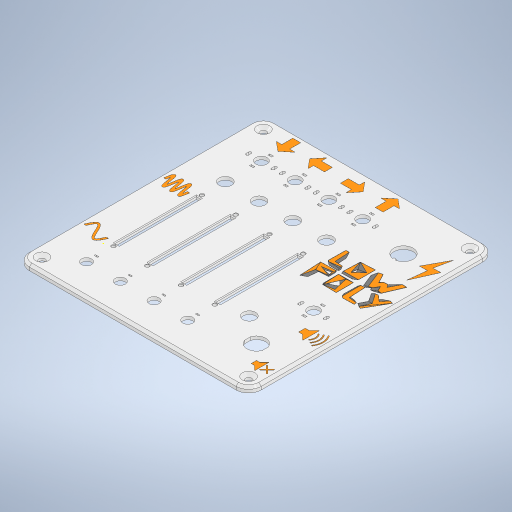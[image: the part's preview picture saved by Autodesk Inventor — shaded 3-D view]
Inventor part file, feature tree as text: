
AUTODESK INVENTOR PART (.ipt)
format: ipt  version: 2024.1 (Build 281209000, 209)  size: 8,110,080 bytes
history: native  units: mm
features: sketch x61, extrude x60, projected_geometry x55, fillet x25, other x13, chamfer x10, plane x2, pattern_linear x2
ambient origin geometry x8: Origin, YZ Plane, XZ Plane, XY Plane, X Axis, Y Axis, Z Axis, Center Point
bodies: Solid12 (feature_tree)
feature tree (228):
  other  "items"
  other  "Blocks"
  extrude  "Extrusion1"  Depth=9.5mm
  extrude  "Extrusion2"  Depth=9.5mm
  extrude  "Extrusion3"  Depth=12.0mm
  extrude  "Extrusion4"  Depth=12.0mm
  extrude  "Extrusion5"  Depth=3.3mm
  extrude  "Extrusion6"  Depth=4.0mm
  extrude  "Extrusion7"  Depth=3.3mm
  extrude  "Extrusion8"  Depth=3.3mm
  extrude  "Extrusion9"  Depth=3.3mm
  extrude  "Extrusion31"  Depth=4.3mm TaperAngle=0.0deg
  fillet  "Fillet1"  Radius=1.76mm
  extrude  "Extrusion10"  Depth=0.57mm
  plane  "Work Plane1"
  extrude  "Extrusion11"  Depth=4.96mm
  extrude  "push-buttons"  Depth=1.22mm
  chamfer  "Chamfer1"  Distance=15.0mm
  extrude  "Extrusion13"  Depth=4.96mm
  fillet  "Fillet3"  Radius=0.49mm
  extrude  "Extrusion14"  Depth=5.0mm TaperAngle=0.0deg
  fillet  "Fillet4"  Radius=1.6mm
  extrude  "toggle-switches"  Depth=56.35mm
  extrude  "Extrusion60"  Depth=5.0mm TaperAngle=0.0deg
  extrude  "Extrusion61"  Depth=15.2mm
  fillet  "Fillet26"  Radius=16.4mm
  extrude  "Extrusion15"  Depth=30.0mm
  extrude  "Extrusion16"  Depth=10.35mm TaperAngle=0.0deg
  extrude  "Extrusion17"  Depth=1.2mm
  extrude  "Extrusion21"  Depth=7.5mm
  extrude  "Extrusion30"  Depth=5.9mm
  fillet  "Fillet5"  Radius=12.0mm
  extrude  "Extrusion18"  Depth=7.65mm
  extrude  "Extrusion19"  Depth=0.74mm
  extrude  "Extrusion20"  Depth=9.1mm
  fillet  "Fillet6"  Radius=4.0mm
  extrude  "Extrusion22"  Depth=20.0mm
  extrude  "faceplate-extrude"  Depth=2.0mm TaperAngle=45.0deg
  fillet  "Fillet7"  Radius=5.48mm
  extrude  "Extrusion24"  Depth=3.0mm TaperAngle=0.0deg
  chamfer  "Chamfer2"  Distance=11.1mm
  chamfer  "Chamfer3"  Distance=12.3mm
  sketch  "Sketch25"  dims[d64=0.5mm d65=7.65mm]
  extrude  "knob-extrude"  Depth=6.8mm
  extrude  "Extrusion26"  Depth=5.9mm
  extrude  "Extrusion27"  Depth=10.0mm TaperAngle=0.0deg
  chamfer  "Chamfer4"  Distance=6.2mm
  chamfer  "Chamfer5"  Distance=28.0mm
  extrude  "Extrusion28"  Depth=17.15mm
  fillet  "Fillet8"  Radius=2.0mm
  chamfer  "Chamfer6"  Distance=1.2mm
  fillet  "Fillet9"  Radius=1.2mm
  extrude  "Extrusion29"  Depth=0.2mm
  fillet  "Fillet10"  Radius=7.5mm
  chamfer  "Chamfer7"  Distance=7.5mm
  fillet  "Fillet11"  Radius=7.5mm
  chamfer  "Chamfer8"  Distance=7.5mm
  chamfer  "Chamfer9"  Distance=7.5mm
  extrude  "Extrusion32"  Depth=0.2mm TaperAngle=0.0deg
  extrude  "Extrusion33"  Depth=0.2mm
  fillet  "Fillet12"  Radius=5.2mm
  chamfer  "Chamfer10"  Distance=0.85mm
  extrude  "Extrusion34"  Depth=0.2mm TaperAngle=0.0deg
  extrude  "bracing"  Depth=0.2mm
  extrude  "graphics-controls"  Depth=0.2mm
  fillet  "Fillet13"  Radius=0.8mm
  fillet  "Fillet14"  Radius=0.1mm
  extrude  "waves"  Depth=0.2mm
  fillet  "Fillet15"  Radius=0.2mm
  fillet  "Fillet16"  Radius=0.3mm
  extrude  "logo"  Depth=0.2mm
  fillet  "Fillet17"  Radius=2.0mm
  extrude  "Extrusion41"  Depth=0.2mm
  extrude  "Extrusion42"  Depth=0.2mm
  extrude  "Extrusion43"  Depth=0.2mm
  extrude  "Extrusion44"  TaperAngle=0.0deg  [1 undecoded]
  fillet  "Fillet18"  Radius=2.0mm
  fillet  "Fillet19"  Radius=0.2mm
  fillet  "Fillet21"  Radius=10.0mm
  extrude  "Extrusion45"  Depth=0.2mm
  extrude  "Extrusion46"  Depth=0.2mm
  extrude  "Extrusion47"  Depth=0.2mm
  fillet  "Fillet20"  Radius=3.98mm
  extrude  "Extrusion48"  Depth=0.2mm
  fillet  "Fillet22"  Radius=10.0mm
  fillet  "Fillet23"  Radius=6.5mm
  plane  "Work Plane2"
  extrude  "Extrusion49"  Depth=0.2mm TaperAngle=0.0deg
  pattern_linear  "Rectangular Pattern1"  Spacing1=4.0mm  [1 undecoded]
  extrude  "Extrusion50"  Depth=0.2mm TaperAngle=45.0deg
  extrude  "Extrusion51"  TaperAngle=0.0deg  [1 undecoded]
  fillet  "Fillet24"  Radius=1.0mm
  extrude  "6.35-jack-hole"  Depth=0.2mm TaperAngle=45.0deg
  extrude  "Extrusion53"  Depth=0.2mm
  extrude  "Extrusion54"  Depth=0.2mm
  extrude  "Extrusion55"  Depth=0.2mm
  fillet  "Fillet25"  Radius=1.8mm
  extrude  "Extrusion56"  Depth=0.2mm
  extrude  "Extrusion57"  Depth=0.2mm
  extrude  "Extrusion58"  Depth=0.2mm
  pattern_linear  "Rectangular Pattern2"  Spacing1=1.0mm  [1 undecoded]
  extrude  "Extrusion62"  TaperAngle=0.0deg  [1 undecoded]
  sketch  "Sketch1"  dims[d0=60.0mm d1=9.5mm]
  sketch  "Sketch2"  dims[d2=9.5mm d3=9.5mm]
  sketch  "Sketch3"  dims[d4=9.5mm d5=12.0mm]
  sketch  "Sketch4"  dims[d6=12.0mm d7=12.0mm]
  projected_geometry  "Projected Loop1"
  sketch  "Sketch5"  dims[d8=6.0mm d9=0.0mm d10=3.3mm]
  projected_geometry  "Projected Loop2"
  projected_geometry  "Projected Loop3"
  projected_geometry  "Projected Loop4"
  sketch  "Sketch6"  dims[d11=3.3mm d12=4.0mm]
  sketch  "Sketch7"  dims[d13=4.0mm d14=3.3mm]
  sketch  "Sketch8"  dims[d15=3.3mm d16=3.3mm]
  sketch  "Sketch9"  dims[d17=3.3mm d18=3.3mm]
  projected_geometry  "Projected Loop5"
  sketch  "Sketch10"  dims[d19=3.3mm d20=4.3mm d21=0.0mm d22=1.76mm]
  projected_geometry  "Projected Loop6"
  sketch  "Sketch11"  dims[d24=2.9mm d25=0.57mm]
  projected_geometry  "Projected Loop7"
  sketch  "Sketch12"  dims[d26=1.97mm d27=4.96mm]
  sketch  "Sketch13"  dims[d28=1.495mm d29=1.22mm]
  sketch  "Sketch14"  dims[d30=0.27mm d31=15.0mm d32=0.0mm]
  sketch  "Sketch15"  dims[d33=3.98mm d34=4.96mm d35=0.49mm]
  sketch  "Sketch16"  dims[d36=5.0mm d37=0.0mm d38=5.0mm d39=0.0mm d40=1.6mm]
  sketch  "Sketch17"  dims[d41=1.825mm d42=56.35mm]
  projected_geometry  "Projected Loop8"
  sketch  "Sketch18"  dims[d43=1.825mm d44=5.0mm d45=0.0mm]
  sketch  "Sketch19"  dims[d46=19.0mm d47=15.2mm d48=16.4mm]
  projected_geometry  "Projected Loop9"
  sketch  "Sketch20"  dims[d49=30.0mm d50=30.0mm]
  projected_geometry  "Projected Loop10"
  sketch  "Sketch21"  dims[d51=30.0mm d53=10.35mm d54=0.0mm]
  projected_geometry  "Projected Loop11"
  projected_geometry  "Projected Loop12"
  projected_geometry  "Projected Loop13"
  projected_geometry  "Projected Loop14"
  projected_geometry  "Projected Loop15"
  projected_geometry  "Projected Loop20"
  projected_geometry  "Projected Loop21"
  sketch  "Sketch22"  dims[d55=6.8mm d56=1.2mm]
  projected_geometry  "Projected Loop22"
  projected_geometry  "Projected Loop23"
  projected_geometry  "Projected Loop24"
  projected_geometry  "Projected Loop25"
  projected_geometry  "Projected Loop26"
  sketch  "Sketch23"  dims[d57=2.87mm d58=7.5mm]
  other  "faceplate"
  sketch  "Sketch24"  dims[d59=4.5mm d60=0.0mm d61=5.9mm d62=12.0mm d63=0.0mm]
  sketch  "Sketch26"  dims[d67=13.0mm d68=0.74mm]
  projected_geometry  "Projected Loop27"
  other  "slider-knob"
  sketch  "Sketch27"  dims[d69=9.2mm d70=0.0mm d71=9.1mm d72=4.0mm d73=-1.745329mm]
  projected_geometry  "Projected Loop28"
  sketch  "Sketch28"  dims[d74=2.0mm d77=20.0mm]
  projected_geometry  "Projected Loop29"
  sketch  "Sketch29"  dims[d78=12.3mm d79=0.0mm d80=2.0mm d81=2.0mm d82=45.0deg d84=5.48mm d85=0.0mm]
  projected_geometry  "Projected Loop30"
  sketch  "Sketch30"  dims[d87=2.0mm d89=3.0mm d90=0.0mm]
  sketch  "Sketch31"  dims[d91=5.0mm d92=11.1mm d93=5.55mm]
  sketch  "Sketch32"  dims[d94=11.1mm]
  projected_geometry  "Projected Loop31"
  projected_geometry  "Projected Loop32"
  projected_geometry  "Projected Loop33"
  projected_geometry  "Projected Loop34"
  projected_geometry  "Projected Loop35"
  projected_geometry  "Projected Loop36"
  projected_geometry  "Projected Loop37"
  projected_geometry  "Projected Loop38"
  projected_geometry  "Projected Loop39"
  projected_geometry  "Projected Loop40"
  projected_geometry  "Projected Loop41"
  projected_geometry  "Projected Loop42"
  projected_geometry  "Projected Loop43"
  projected_geometry  "Projected Loop45"
  sketch  "Sketch33"  dims[d95=5.55mm]
  sketch  "Sketch34"  dims[d96=11.1mm]
  sketch  "Sketch35"  dims[d98=11.1mm]
  projected_geometry  "Projected Loop46"
  projected_geometry  "Projected Loop47"
  projected_geometry  "Projected Loop48"
  projected_geometry  "Projected Loop49"
  projected_geometry  "Projected Loop50"
  projected_geometry  "Projected Loop51"
  projected_geometry  "Projected Loop52"
  projected_geometry  "Projected Loop53"
  projected_geometry  "Projected Loop54"
  projected_geometry  "Projected Loop55"
  projected_geometry  "Projected Loop56"
  sketch  "Sketch36"  dims[d99=5.55mm]
  sketch  "Sketch38"  dims[d100=11.1mm]
  other  "2D Equation Curve1"
  sketch  "Sketch40"  dims[d101=5.55mm]
  other  "2D Equation Curve2"
  other  "2D Equation Curve4"
  other  "low-poly-logo"
  sketch  "Sketch42"  dims[d102=10.7mm]
  other  "000-low-poly-logo"
  sketch  "Sketch43"  dims[d103=10.7mm]
  projected_geometry  "Projected Loop57"
  other  "case-body"
  sketch  "Sketch44"  dims[d104=15.2mm]
  projected_geometry  "Projected Loop58"
  sketch  "Sketch45"  dims[d105=15.2mm]
  projected_geometry  "Projected Loop59"
  projected_geometry  "Projected Loop60"
  sketch  "Sketch46"  dims[d108=23.0mm]
  sketch  "Sketch47"  dims[d109=17.0mm d110=12.3mm d111=0.0mm]
  other  "circuit-boards"
  sketch  "Sketch48"  dims[d112=6.8mm d113=6.8mm]
  sketch  "Sketch49"  dims[d114=10.0mm d115=0.0mm d116=5.9mm]
  sketch  "Sketch50"  dims[d117=5.9mm d118=10.0mm d119=0.0mm]
  sketch  "Sketch51"  dims[d120=0.2mm]
  sketch  "Sketch52"  dims[d121=11.9mm d122=6.2mm d123=0.0mm]
  sketch  "Sketch53"  dims[d124=16.0mm]
  sketch  "Sketch54"  dims[d125=29.0mm]
  sketch  "Sketch55"  dims[d126=14.5mm]
  other  "jacks"
  sketch  "Sketch56"  dims[d127=8.0mm d128=28.0mm d129=0.0mm]
  sketch  "Sketch57"  dims[d130=4.8mm d131=17.15mm d132=0.523599mm d133=2.0mm]
  sketch  "Sketch58"  dims[d134=20.0mm]
  sketch  "Sketch59"  dims[d135=26.0mm]
  sketch  "Sketch60"  dims[d136=16.0mm]
  sketch  "Sketch61"  dims[d138=1.2mm]
  sketch  "Sketch62"  dims[d139=2.87mm]
  sketch  "Sketch63"  dims[d140=1.2mm]
  sketch  "Sketch64"  dims[d141=1.2mm d142=1.2mm d143=1.2mm d144=2.87mm d145=7.5mm d146=7.5mm d147=7.5mm d148=7.5mm d149=7.5mm d150=17.15mm d151=0.0mm d152=1.7mm d153=5.2mm d154=0.85mm d155=10.0mm d156=0.0mm d158=0.2mm d159=0.2mm d160=0.8mm d161=0.1mm d162=0.1mm d163=0.2mm d164=0.3mm d165=0.25mm d167=2.0mm d168=0.0mm d169=0.2mm d170=8.0mm d171=4.0mm d172=0.0mm d173=0.0mm d174=2.0mm d175=2.0mm d176=45.0deg d177=0.2mm d178=2.0mm d179=45.0deg d180=10.0mm d181=22.0mm d182=1.76mm d183=4.12mm d184=3.98mm d185=9.01mm d186=10.0mm d187=0.0mm d188=6.5mm d189=0.0mm d190=2.5mm d191=0.0mm d192=4.0mm d193=2.0mm d194=45.0deg d195=2.5mm d196=9.0mm d197=45.0deg d198=0.0mm d199=0.0mm d200=1.0mm d201=2.5mm d202=9.0mm d203=45.0deg d204=2.0mm d205=0.9mm d206=1.2mm d207=1.8mm d208=1.3mm d209=2.0mm d210=1.5mm d211=1.0mm d212=0.0mm d213=0.0mm d214=0.4mm d215=3.341737mm d216=2.5mm d217=9.0mm d218=45.0deg d219=0.5mm d221=7.5mm d222=7.5mm d223=7.5mm d224=7.5mm d225=1.2mm d226=1.2mm d227=1.2mm d228=1.2mm d229=5.5mm d230=1.9mm d231=0.77mm d232=1.9mm d233=0.77mm d234=1.9mm d235=0.77mm d236=1.9mm d237=0.77mm d238=1.9mm d239=0.77mm d240=1.9mm d241=0.77mm d242=1.9mm d243=0.77mm d244=1.9mm d245=0.77mm d246=5.5mm d247=1.4mm d248=0.0mm d249=1.2mm d253=1.2mm d255=7.5mm d256=2.87mm d257=1.9mm d258=0.77mm d259=1.9mm d260=0.77mm d261=11.0mm d262=5.5mm d263=1.4mm d264=0.0mm d265=0.2mm d266=0.5mm d267=2.0mm d268=45.0deg d269=1.5mm d270=2.0mm d271=45.0deg d273=1.5mm d274=0.5mm d275=0.0mm d276=25.0mm d277=0.4mm d278=0.0mm d279=2.0mm d280=0.4mm d281=2.0mm d282=45.0deg d283=12.0mm d284=1.5mm d285=0.0mm d286=1.5mm d287=0.0mm d304=7.0mm d314=5.0mm d315=5.0mm d316=12.0mm d317=2.0mm d318=12.0mm d319=7.0mm d320=7.0mm d321=5.0mm d322=5.0mm d323=5.0mm d324=5.0mm d325=7.0mm d326=5.0mm d327=5.0mm d328=12.0mm d329=12.0mm d330=3.0mm d331=4.2mm d332=3.36mm d333=2.52mm d334=3.36mm d335=10.92mm d336=0.672mm d337=2.94mm d338=2.94mm d339=4.116mm d340=4.116mm d341=5.208mm d342=0.672mm d343=0.672mm d344=1.68mm d345=1.68mm d346=1.68mm d347=3.36mm d348=2.94mm d349=2.1mm d350=2.94mm d351=13.0mm d363=45.0deg d364=90.0deg d365=3.36mm d366=0.756mm d367=0.756mm d368=2.1mm d369=2.1mm d370=0.0mm d371=10.0mm d372=0.05mm d373=0.0mm d374=0.1mm d375=0.05mm d376=0.0mm d377=10.0mm d380=0.0mm d381=3600.0mm d390=0.0mm d391=10800.0mm d394=0.0mm d395=10800.0mm d396=1.5mm d397=1.0mm d398=3.0mm d400=0.0mm d401=3600.0mm d402=1.5mm d403=3.0mm d404=1.0mm d405=0.05mm d406=0.0mm d407=1.0mm d408=0.15mm d422=5.208mm d426=0.05mm d427=0.0mm d428=60.0mm d429=32.0mm d430=0.1mm d431=0.1mm d432=0.1mm d435=0.1mm d437=30.0mm d438=0.0mm d439=0.4mm d440=2.0mm d441=2.0mm d442=0.0mm d443=2.0mm d444=0.0mm d445=43.0mm d446=55.0mm d447=3.0mm d448=3.0mm d449=6.0mm d450=0.0mm d451=2.0mm d452=5.0mm d453=43.0mm d454=55.0mm d455=3.0mm d456=3.0mm d457=3.0mm d458=4.0mm d459=0.0mm d460=10.1mm d461=19.1mm d462=11.2mm d463=23.0mm d464=7.0mm d465=0.0mm d466=16.4mm d469=32.0mm d470=0.0mm d471=1.0mm d473=4.12mm d474=5.5mm d475=1.0mm d476=0.5mm d477=3.2mm d478=5.0mm d479=3.0mm d481=5.0mm d482=5.0mm d483=5.0mm d484=3.0mm d485=4.0mm d486=4.0mm d487=5.0mm d488=8.0mm d489=44.0mm d490=0.0mm d491=0.0mm d492=260.0mm d493=3.0mm d494=30.0mm d495=11.5mm d496=11.5mm d497=3.0mm d498=0.0mm d499=30.0mm d501=11.0mm d502=5.0mm d503=4.0mm d504=6.0mm d505=0.0mm d506=4.999995mm d507=5.0mm d508=1.5mm d509=1.499992mm d510=3.0mm d511=1.5mm d512=5.0mm d513=6.0mm d514=28.0mm d515=0.0mm d516=0.0mm d517=200.0mm d518=11.0mm d519=20.0mm d520=8.0mm d521=22.0mm d522=6.0mm d523=0.0mm d524=10.83mm d525=8.5mm d526=0.0mm d527=6.5mm d528=20.1mm d529=10.05mm d530=7.9mm d531=14.8mm d532=26.0mm d533=0.0mm d534=0.4mm d535=0.4mm d536=1.3mm d537=1.3mm d538=1.3mm d539=3.4mm d540=2.0mm d541=2.0mm d542=5.05mm d543=5.05mm d544=4.5mm d545=0.0mm d546=0.6mm d547=24.0mm d548=14.0mm d549=11.5mm d550=0.0mm d551=0.0mm d552=18.0mm d553=22.0mm d554=0.0mm d556=3.0mm d557=22.0mm d558=0.0mm d559=20.0mm d561=131.6mm d562=20.0mm d564=141.0mm d565=12.06mm d566=7.06mm d567=12.77mm d568=9.0mm d569=7.06mm d570=12.77mm d571=7.06mm d572=12.77mm d573=7.06mm d574=12.77mm d575=13.05mm d576=0.0mm d577=6.1mm d578=5.5mm d579=0.0mm d580=2.5mm d581=10.8mm d582=0.349066mm d583=1.0mm d584=18.35mm d585=35.0mm d586=0.15mm d587=8.4mm d588=8.4mm d589=2.2mm d590=0.9mm d591=6.3mm d592=0.0mm d593=0.0mm]
  other  "000-low-poly-logo:1"
note: 5 required parameter values undecoded (feature->parameter linkage not recoverable at this tier; creation-order binding heuristic only, values carry confidence <= 0.55)
